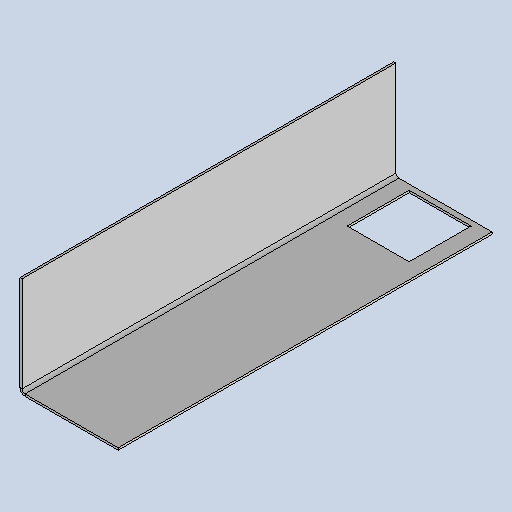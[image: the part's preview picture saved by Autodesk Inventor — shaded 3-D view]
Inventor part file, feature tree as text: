
AUTODESK INVENTOR PART (.ipt)
format: ipt  version: 2025.1 (Build 291241020, 241B)  size: 169,984 bytes
history: native  units: mm
features: sheet_metal_op x4, other x4, sketch x3
ambient origin geometry x8: Origin, YZ Plane, XZ Plane, XY Plane, X Axis, Y Axis, Z Axis, Center Point
bodies: Body1 (feature_tree)
feature tree (11):
  sheet_metal_op  "Face3"
  sheet_metal_op  "Flange3"
  sketch  "Sketch1"  dims[d154=92.0mm]
  other  "Plate5"
  sketch  "Sketch7"  dims[d155=350.0mm]
  other  "Plate6"
  sheet_metal_op  "Bend3"
  sheet_metal_op  "Corner3"
  sketch  "Sketch8"  dims[d156=2.0mm d157=2.0mm d158=1.0mm d159=4.0mm d160=2.75mm d161=94.0mm d162=90.0deg d163=2.75mm d164=8.0mm d165=2.0mm d166=2.75mm d167=58.0mm d168=58.0mm d169=5.0mm d170=2.0mm d171=0.0mm]
  other  "Cut1"
  other  "Definition1"
